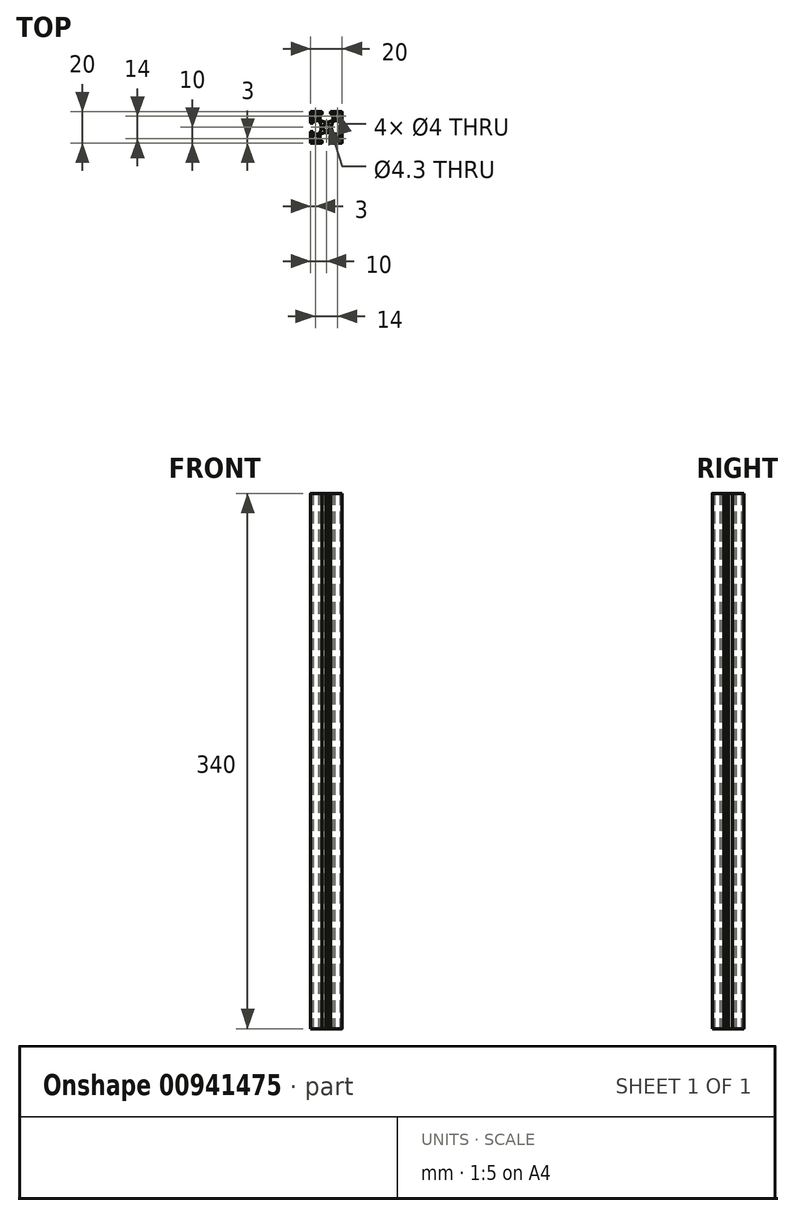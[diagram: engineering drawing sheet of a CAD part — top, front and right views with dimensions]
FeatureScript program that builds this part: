
annotation { "Feature Type Name" : "Feature", "Feature Type Description" : "" }
export const myFeature = defineFeature(function(context is Context, id is Id, definition is map)
    precondition{}
    {
        {
            var Q0;
            Q0=qCreatedBy(makeId("Top.planeOp"),FACE);
            var sketch = newSketch(context, id + "F0", { "sketchPlane" : qUnion([Q0])});
            skLineSegment(sketch, "E0", {"start": v(-11.2, 0) * mm, "end": v(11.2, 0) * mm});
            skCircle(sketch, "E1", {"center": v(0, 0) * mm, "radius": 2.15 * mm});
            skLineSegment(sketch, "E2", {"start": v(4.15, 4.94) * mm, "end": v(4.15, 8.2) * mm});
            skArc(sketch, "E3", {"start": v(4.15, 8.2) * mm, "mid": v(4.06, 8.41) * mm, "end": v(3.85, 8.5) * mm});
            skLineSegment(sketch, "E4", {"start": v(3.85, 8.5) * mm, "end": v(2.95, 8.5) * mm});
            skArc(sketch, "E5", {"start": v(2.95, 8.5) * mm, "mid": v(2.74, 8.59) * mm, "end": v(2.65, 8.8) * mm});
            skLineSegment(sketch, "E6", {"start": v(2.65, 8.8) * mm, "end": v(2.65, 9.7) * mm});
            skArc(sketch, "E7", {"start": v(2.65, 9.7) * mm, "mid": v(2.74, 9.91) * mm, "end": v(2.95, 10) * mm});
            skLineSegment(sketch, "E8", {"start": v(2.95, 10) * mm, "end": v(9.7, 10) * mm});
            skArc(sketch, "E9", {"start": v(9.7, 10) * mm, "mid": v(9.91, 9.91) * mm, "end": v(10, 9.7) * mm});
            skLineSegment(sketch, "E10", {"start": v(10, 9.7) * mm, "end": v(10, 2.95) * mm});
            skArc(sketch, "E11", {"start": v(10, 2.95) * mm, "mid": v(9.91, 2.74) * mm, "end": v(9.7, 2.65) * mm});
            skLineSegment(sketch, "E12", {"start": v(9.7, 2.65) * mm, "end": v(8.8, 2.65) * mm});
            skArc(sketch, "E13", {"start": v(8.8, 2.65) * mm, "mid": v(8.59, 2.74) * mm, "end": v(8.5, 2.95) * mm});
            skLineSegment(sketch, "E14", {"start": v(8.5, 2.95) * mm, "end": v(8.5, 3.85) * mm});
            skArc(sketch, "E15", {"start": v(8.5, 3.85) * mm, "mid": v(8.41, 4.06) * mm, "end": v(8.2, 4.15) * mm});
            skLineSegment(sketch, "E16", {"start": v(8.2, 4.15) * mm, "end": v(4.94, 4.15) * mm});
            skArc(sketch, "E17", {"start": v(4.94, 4.15) * mm, "mid": v(4.81, 4.12) * mm, "end": v(4.7, 4.04) * mm});
            skArc(sketch, "E18", {"start": v(4.7, 4.04) * mm, "mid": v(3.71, 2.28) * mm, "end": v(3.3, 0.3) * mm});
            skLineSegment(sketch, "E19", {"start": v(3.3, 0.3) * mm, "end": v(3, 0) * mm});
            skLineSegment(sketch, "E20", {"start": v(3, 0) * mm, "end": v(3.3, -0.3) * mm});
            skArc(sketch, "E21", {"start": v(3.3, -0.3) * mm, "mid": v(3.71, -2.28) * mm, "end": v(4.7, -4.04) * mm});
            skArc(sketch, "E22", {"start": v(4.7, -4.04) * mm, "mid": v(4.81, -4.12) * mm, "end": v(4.94, -4.15) * mm});
            skLineSegment(sketch, "E23", {"start": v(4.94, -4.15) * mm, "end": v(8.2, -4.15) * mm});
            skArc(sketch, "E24", {"start": v(8.2, -4.15) * mm, "mid": v(8.41, -4.06) * mm, "end": v(8.5, -3.85) * mm});
            skLineSegment(sketch, "E25", {"start": v(8.5, -3.85) * mm, "end": v(8.5, -2.95) * mm});
            skArc(sketch, "E26", {"start": v(8.5, -2.95) * mm, "mid": v(8.59, -2.74) * mm, "end": v(8.8, -2.65) * mm});
            skLineSegment(sketch, "E27", {"start": v(8.8, -2.65) * mm, "end": v(9.7, -2.65) * mm});
            skArc(sketch, "E28", {"start": v(9.7, -2.65) * mm, "mid": v(9.91, -2.74) * mm, "end": v(10, -2.95) * mm});
            skLineSegment(sketch, "E29", {"start": v(10, -2.95) * mm, "end": v(10, -9.7) * mm});
            skArc(sketch, "E30", {"start": v(10, -9.7) * mm, "mid": v(9.91, -9.91) * mm, "end": v(9.7, -10) * mm});
            skLineSegment(sketch, "E31", {"start": v(9.7, -10) * mm, "end": v(2.95, -10) * mm});
            skArc(sketch, "E32", {"start": v(2.95, -10) * mm, "mid": v(2.74, -9.91) * mm, "end": v(2.65, -9.7) * mm});
            skLineSegment(sketch, "E33", {"start": v(2.65, -9.7) * mm, "end": v(2.65, -8.8) * mm});
            skArc(sketch, "E34", {"start": v(2.65, -8.8) * mm, "mid": v(2.74, -8.59) * mm, "end": v(2.95, -8.5) * mm});
            skLineSegment(sketch, "E35", {"start": v(2.95, -8.5) * mm, "end": v(3.85, -8.5) * mm});
            skArc(sketch, "E36", {"start": v(3.85, -8.5) * mm, "mid": v(4.06, -8.41) * mm, "end": v(4.15, -8.2) * mm});
            skLineSegment(sketch, "E37", {"start": v(4.15, -8.2) * mm, "end": v(4.15, -4.94) * mm});
            skArc(sketch, "E38", {"start": v(4.15, -4.94) * mm, "mid": v(4.12, -4.81) * mm, "end": v(4.04, -4.7) * mm});
            skArc(sketch, "E39", {"start": v(4.04, -4.7) * mm, "mid": v(2.28, -3.71) * mm, "end": v(0.3, -3.3) * mm});
            skLineSegment(sketch, "E40", {"start": v(0.3, -3.3) * mm, "end": v(0, -3) * mm});
            skLineSegment(sketch, "E41", {"start": v(0, -3) * mm, "end": v(-0.3, -3.3) * mm});
            skArc(sketch, "E42", {"start": v(-0.3, -3.3) * mm, "mid": v(-2.28, -3.71) * mm, "end": v(-4.04, -4.7) * mm});
            skArc(sketch, "E43", {"start": v(-4.04, -4.7) * mm, "mid": v(-4.12, -4.81) * mm, "end": v(-4.15, -4.94) * mm});
            skLineSegment(sketch, "E44", {"start": v(-4.15, -4.94) * mm, "end": v(-4.15, -8.2) * mm});
            skArc(sketch, "E45", {"start": v(-4.15, -8.2) * mm, "mid": v(-4.06, -8.41) * mm, "end": v(-3.85, -8.5) * mm});
            skLineSegment(sketch, "E46", {"start": v(-3.85, -8.5) * mm, "end": v(-2.95, -8.5) * mm});
            skArc(sketch, "E47", {"start": v(-2.95, -8.5) * mm, "mid": v(-2.74, -8.59) * mm, "end": v(-2.65, -8.8) * mm});
            skLineSegment(sketch, "E48", {"start": v(-2.65, -8.8) * mm, "end": v(-2.65, -9.7) * mm});
            skArc(sketch, "E49", {"start": v(-2.65, -9.7) * mm, "mid": v(-2.74, -9.91) * mm, "end": v(-2.95, -10) * mm});
            skLineSegment(sketch, "E50", {"start": v(-2.95, -10) * mm, "end": v(-9.7, -10) * mm});
            skArc(sketch, "E51", {"start": v(-9.7, -10) * mm, "mid": v(-9.91, -9.91) * mm, "end": v(-10, -9.7) * mm});
            skLineSegment(sketch, "E52", {"start": v(-10, -9.7) * mm, "end": v(-10, -2.95) * mm});
            skArc(sketch, "E53", {"start": v(-10, -2.95) * mm, "mid": v(-9.91, -2.74) * mm, "end": v(-9.7, -2.65) * mm});
            skLineSegment(sketch, "E54", {"start": v(-9.7, -2.65) * mm, "end": v(-8.8, -2.65) * mm});
            skArc(sketch, "E55", {"start": v(-8.8, -2.65) * mm, "mid": v(-8.59, -2.74) * mm, "end": v(-8.5, -2.95) * mm});
            skLineSegment(sketch, "E56", {"start": v(-8.5, -2.95) * mm, "end": v(-8.5, -3.85) * mm});
            skArc(sketch, "E57", {"start": v(-8.5, -3.85) * mm, "mid": v(-8.41, -4.06) * mm, "end": v(-8.2, -4.15) * mm});
            skLineSegment(sketch, "E58", {"start": v(-8.2, -4.15) * mm, "end": v(-4.94, -4.15) * mm});
            skArc(sketch, "E59", {"start": v(-4.94, -4.15) * mm, "mid": v(-4.81, -4.12) * mm, "end": v(-4.7, -4.04) * mm});
            skArc(sketch, "E60", {"start": v(-4.7, -4.04) * mm, "mid": v(-3.71, -2.28) * mm, "end": v(-3.3, -0.3) * mm});
            skLineSegment(sketch, "E61", {"start": v(-3.3, -0.3) * mm, "end": v(-3, 0) * mm});
            skLineSegment(sketch, "E62", {"start": v(-3, 0) * mm, "end": v(-3.3, 0.3) * mm});
            skArc(sketch, "E63", {"start": v(-3.3, 0.3) * mm, "mid": v(-3.71, 2.28) * mm, "end": v(-4.7, 4.04) * mm});
            skArc(sketch, "E64", {"start": v(-4.7, 4.04) * mm, "mid": v(-4.81, 4.12) * mm, "end": v(-4.94, 4.15) * mm});
            skLineSegment(sketch, "E65", {"start": v(-4.94, 4.15) * mm, "end": v(-8.2, 4.15) * mm});
            skArc(sketch, "E66", {"start": v(-8.2, 4.15) * mm, "mid": v(-8.41, 4.06) * mm, "end": v(-8.5, 3.85) * mm});
            skLineSegment(sketch, "E67", {"start": v(-8.5, 3.85) * mm, "end": v(-8.5, 2.95) * mm});
            skArc(sketch, "E68", {"start": v(-8.5, 2.95) * mm, "mid": v(-8.59, 2.74) * mm, "end": v(-8.8, 2.65) * mm});
            skLineSegment(sketch, "E69", {"start": v(-8.8, 2.65) * mm, "end": v(-9.7, 2.65) * mm});
            skArc(sketch, "E70", {"start": v(-9.7, 2.65) * mm, "mid": v(-9.91, 2.74) * mm, "end": v(-10, 2.95) * mm});
            skLineSegment(sketch, "E71", {"start": v(-10, 2.95) * mm, "end": v(-10, 9.7) * mm});
            skArc(sketch, "E72", {"start": v(-10, 9.7) * mm, "mid": v(-9.91, 9.91) * mm, "end": v(-9.7, 10) * mm});
            skLineSegment(sketch, "E73", {"start": v(-9.7, 10) * mm, "end": v(-2.95, 10) * mm});
            skArc(sketch, "E74", {"start": v(-2.95, 10) * mm, "mid": v(-2.74, 9.91) * mm, "end": v(-2.65, 9.7) * mm});
            skLineSegment(sketch, "E75", {"start": v(-2.65, 9.7) * mm, "end": v(-2.65, 8.8) * mm});
            skArc(sketch, "E76", {"start": v(-2.65, 8.8) * mm, "mid": v(-2.74, 8.59) * mm, "end": v(-2.95, 8.5) * mm});
            skLineSegment(sketch, "E77", {"start": v(-2.95, 8.5) * mm, "end": v(-3.85, 8.5) * mm});
            skArc(sketch, "E78", {"start": v(-3.85, 8.5) * mm, "mid": v(-4.06, 8.41) * mm, "end": v(-4.15, 8.2) * mm});
            skLineSegment(sketch, "E79", {"start": v(-4.15, 8.2) * mm, "end": v(-4.15, 4.94) * mm});
            skArc(sketch, "E80", {"start": v(-4.15, 4.94) * mm, "mid": v(-4.12, 4.81) * mm, "end": v(-4.04, 4.7) * mm});
            skArc(sketch, "E81", {"start": v(-4.04, 4.7) * mm, "mid": v(-2.28, 3.71) * mm, "end": v(-0.3, 3.3) * mm});
            skLineSegment(sketch, "E82", {"start": v(-0.3, 3.3) * mm, "end": v(0, 3) * mm});
            skLineSegment(sketch, "E83", {"start": v(0, 3) * mm, "end": v(0.3, 3.3) * mm});
            skArc(sketch, "E84", {"start": v(0.3, 3.3) * mm, "mid": v(2.28, 3.71) * mm, "end": v(4.04, 4.7) * mm});
            skArc(sketch, "E85", {"start": v(4.04, 4.7) * mm, "mid": v(4.12, 4.81) * mm, "end": v(4.15, 4.94) * mm});
            skLineSegment(sketch, "E86", {"start": v(-9.5, 7) * mm, "end": v(-4.5, 7) * mm});
            skLineSegment(sketch, "E87", {"start": v(-7, 9.5) * mm, "end": v(-7, 4.5) * mm});
            skCircle(sketch, "E88", {"center": v(-7, 7) * mm, "radius": 2 * mm});
            skLineSegment(sketch, "E89", {"start": v(-9.5, -7) * mm, "end": v(-4.5, -7) * mm});
            skLineSegment(sketch, "E90", {"start": v(-7, -9.5) * mm, "end": v(-7, -4.5) * mm});
            skCircle(sketch, "E91", {"center": v(-7, -7) * mm, "radius": 2 * mm});
            skLineSegment(sketch, "E92", {"start": v(0, 11.2) * mm, "end": v(0, -11.2) * mm});
            skLineSegment(sketch, "E93", {"start": v(9.5, 7) * mm, "end": v(4.5, 7) * mm});
            skLineSegment(sketch, "E94", {"start": v(7, 9.5) * mm, "end": v(7, 4.5) * mm});
            skCircle(sketch, "E95", {"center": v(7, 7) * mm, "radius": 2 * mm});
            skCircle(sketch, "E96", {"center": v(7, -7) * mm, "radius": 2 * mm});
            skLineSegment(sketch, "E97", {"start": v(7, -9.5) * mm, "end": v(7, -4.5) * mm});
            skLineSegment(sketch, "E98", {"start": v(9.5, -7) * mm, "end": v(4.5, -7) * mm});
            skSolve(sketch);
        }
        {
            var Q0;
            {var subQ0=sQuery(id+"F0.wireOp",EDGE,"E62");Q0=makeQuery(id+"F0.imprint","IMPRINT",FACE,{"disambiguationData":[TD([[makeQuery(id+"F0.imprint","IMPRINT",EDGE,{"derivedFrom":subQ0}),-1.0]])]});}
            var Q1;
            Q1=makeQuery(id+"F0.imprint","IMPRINT",FACE,{"disambiguationData":[TD([[makeQuery(id+"F0.imprint","IMPRINT",EDGE,{"derivedFrom":sQuery(id+"F0.wireOp",EDGE,"E2")}),-1.0]])]});
            var Q2;
            {var subQ10=sQuery(id+"F0.wireOp",EDGE,"E20");Q2=makeQuery(id+"F0.imprint","IMPRINT",FACE,{"disambiguationData":[TD([[makeQuery(id+"F0.imprint","IMPRINT",EDGE,{"derivedFrom":subQ10}),-1.0]])]});}
            var Q3;
            {var subQ1=sQuery(id+"F0.wireOp",EDGE,"E41");Q3=makeQuery(id+"F0.imprint","IMPRINT",FACE,{"disambiguationData":[TD([[makeQuery(id+"F0.imprint","IMPRINT",EDGE,{"derivedFrom":subQ1}),-1.0]])]});}
            extrude(context, id + "F1", {"entities" : qUnion([Q0, Q1, Q2, Q3]), "depth" : 340 * mm, "offsetDistance" : 25 * mm});
        }
    });
